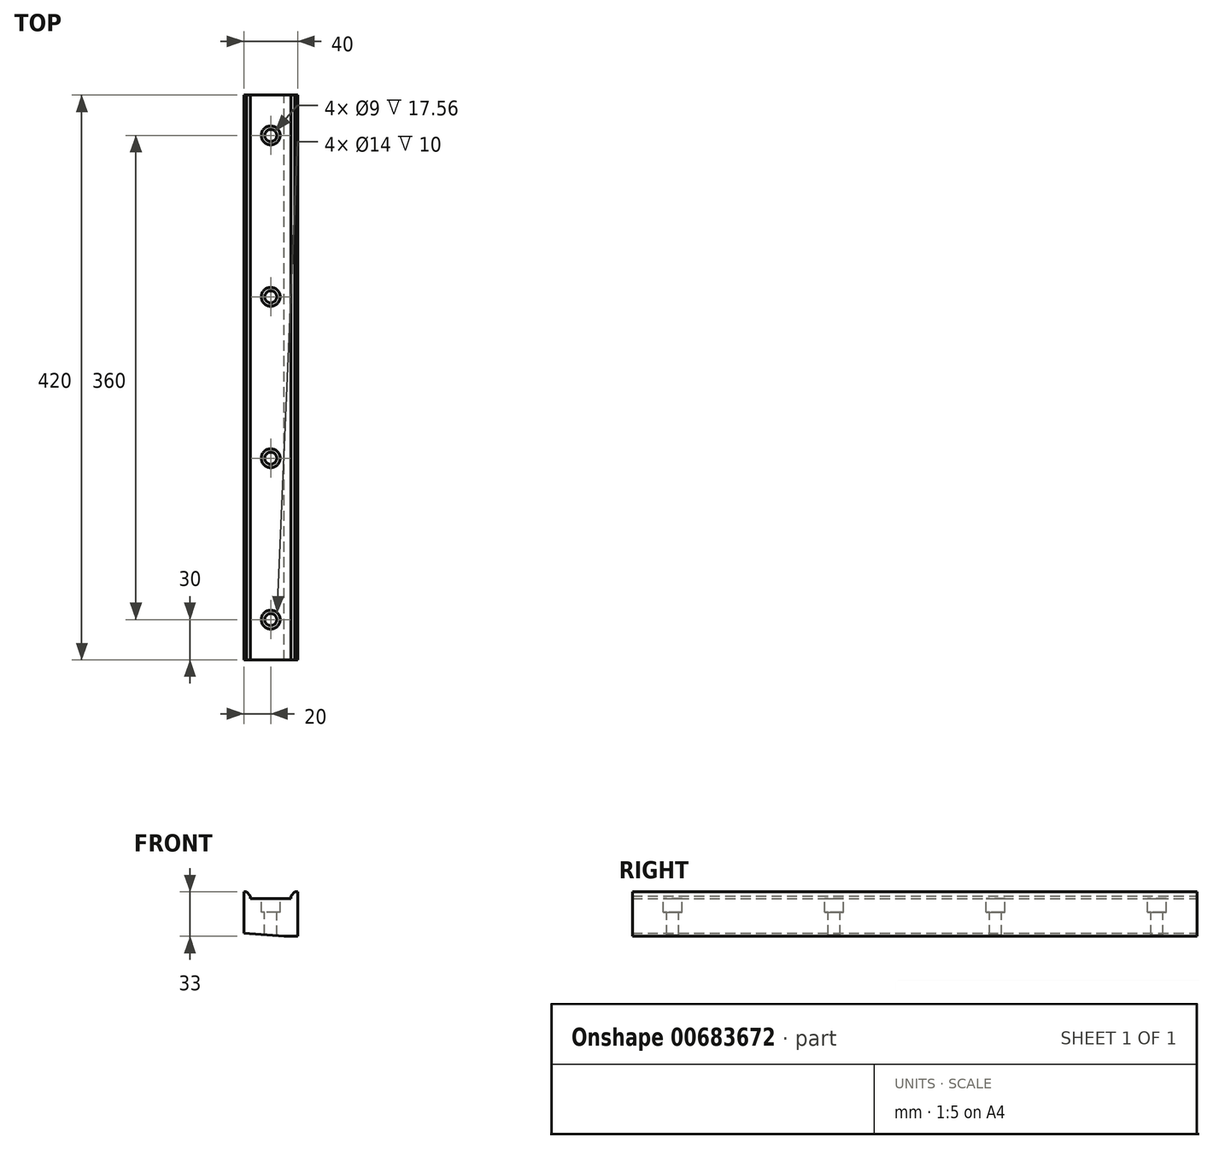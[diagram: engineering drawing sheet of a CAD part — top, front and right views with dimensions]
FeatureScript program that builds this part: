
annotation { "Feature Type Name" : "Feature", "Feature Type Description" : "" }
export const myFeature = defineFeature(function(context is Context, id is Id, definition is map)
    precondition{}
    {
        {
            var Q0;
            Q0=qCreatedBy(makeId("Front.planeOp"),FACE);
            var sketch = newSketch(context, id + "F0", { "sketchPlane" : qUnion([Q0])});
            skLineSegment(sketch, "E0.bottom", {"start": v(30, 0) * mm, "end": v(40, 0) * mm});
            skLineSegment(sketch, "E0.top", {"start": v(0, 33) * mm, "end": v(5, 33) * mm});
            skLineSegment(sketch, "E0.left", {"start": v(0, 2.4) * mm, "end": v(0, 33) * mm});
            skLineSegment(sketch, "E0.right", {"start": v(40, 0) * mm, "end": v(40, 33) * mm});
            skLineSegment(sketch, "E1.0", {"start": v(5, 28) * mm, "end": v(5, 33) * mm});
            skLineSegment(sketch, "E2.0", {"start": v(35, 28) * mm, "end": v(35, 33) * mm});
            skLineSegment(sketch, "E3.0", {"start": v(5, 28) * mm, "end": v(35, 28) * mm});
            skLineSegment(sketch, "E4.trimOffspring", {"start": v(35, 33) * mm, "end": v(40, 33) * mm});
            skLineSegment(sketch, "E5", {"start": v(30, 0) * mm, "end": v(0, 2.4) * mm});
            skPoint(sketch, "E6.orphan", {"position": v(0, 0) * mm});
            skSolve(sketch);
        }
        {
            var Q0;
            Q0=makeQuery(id+"F0.imprint","IMPRINT",FACE,{"disambiguationData":[TD([[makeQuery(id+"F0.imprint","IMPRINT",EDGE,{"derivedFrom":sQuery(id+"F0.wireOp",EDGE,"E0.bottom")}),1.0]])]});
            extrude(context, id + "F1", {"entities" : qUnion([Q0]), "depth" : 420 * mm, "offsetDistance" : 25 * mm});
        }
        {
            var Q0;
            Q0=makeQuery(id+"F1.opExtrude","SWEPT_EDGE",EDGE,{"disambiguationData":[OSD([sQuery(id+"F0.wireOp",EDGE,"E0.top"),sQuery(id+"F0.wireOp",EDGE,"E1.0")])]});
            var Q1;
            Q1=makeQuery(id+"F1.opExtrude","SWEPT_EDGE",EDGE,{"disambiguationData":[OSD([sQuery(id+"F0.wireOp",EDGE,"E2.0"),sQuery(id+"F0.wireOp",EDGE,"E4.trimOffspring")])]});
            chamfer(context, id + "F2", {"entities" : qUnion([Q0, Q1]), "width" : 3 * mm, "tangentPropagation" : true});
        }
        {
            var Q0;
            Q0=makeQuery(id+"F1.opExtrude","SWEPT_FACE",FACE,{"disambiguationData":[OSD([sQuery(id+"F0.wireOp",EDGE,"E3.0")])]});
            var sketch = newSketch(context, id + "F3", { "sketchPlane" : qUnion([Q0])});
            skPoint(sketch, "E7", {"position": v(20, -390) * mm});
            skPoint(sketch, "E8.0.1.0", {"position": v(20, -270) * mm});
            skPoint(sketch, "E8.0.2.0", {"position": v(20, -150) * mm});
            skPoint(sketch, "E8.0.3.0", {"position": v(20, -30) * mm});
            skPoint(sketch, "E8.1.0.0", {"position": v(45, -390) * mm});
            skPoint(sketch, "E8.1.1.0", {"position": v(45, -270) * mm});
            skPoint(sketch, "E8.1.2.0", {"position": v(45, -150) * mm});
            skPoint(sketch, "E8.1.3.0", {"position": v(45, -30) * mm});
            skPoint(sketch, "E8.2.0.0", {"position": v(70, -390) * mm});
            skPoint(sketch, "E8.2.1.0", {"position": v(70, -270) * mm});
            skPoint(sketch, "E8.2.2.0", {"position": v(70, -150) * mm});
            skPoint(sketch, "E8.2.3.0", {"position": v(70, -30) * mm});
            skLineSegment(sketch, "E8.direction1", {"start": v(20, -390) * mm, "end": v(45, -390) * mm, "construction": true});
            skLineSegment(sketch, "E8.direction2", {"start": v(20, -390) * mm, "end": v(20, -270) * mm, "construction": true});
            skSolve(sketch);
        }
        {
            var Q0;
            Q0=sQuery(id+"F3.wireOp",VERTEX,"E7");
            var Q1;
            Q1=sQuery(id+"F3.wireOp",VERTEX,"E8.0.1.0");
            var Q2;
            Q2=sQuery(id+"F3.wireOp",VERTEX,"E8.0.2.0");
            var Q3;
            Q3=sQuery(id+"F3.wireOp",VERTEX,"E8.0.3.0");
            var Q4;
            Q4=makeQuery(id+"F1.opExtrude","SWEPT_BODY",BODY,{"disambiguationData":[OSD([sQuery(id+"F0.wireOp",EDGE,"E0.bottom"),sQuery(id+"F0.wireOp",EDGE,"E0.top"),sQuery(id+"F0.wireOp",EDGE,"E0.left"),sQuery(id+"F0.wireOp",EDGE,"E0.right"),sQuery(id+"F0.wireOp",EDGE,"E1.0"),sQuery(id+"F0.wireOp",EDGE,"E2.0"),sQuery(id+"F0.wireOp",EDGE,"E3.0"),sQuery(id+"F0.wireOp",EDGE,"E4.trimOffspring"),sQuery(id+"F0.wireOp",EDGE,"E5")])]});
            hole(context, id + "F4", {"style" : HoleStyle.C_BORE, "endStyle" : HoleEndStyle.THROUGH, "holeDiameter" : 9 * mm, "cBoreDiameter" : 14 * mm, "cBoreDepth" : 10 * mm, "majorDiameter" : 16 * mm, "isTappedThrough" : true, "tappedDepth" : 30 * mm, "tapClearance" : 2, "locations" : qUnion([Q0, Q1, Q2, Q3]), "scope" : qUnion([Q4])});
        }
    });
